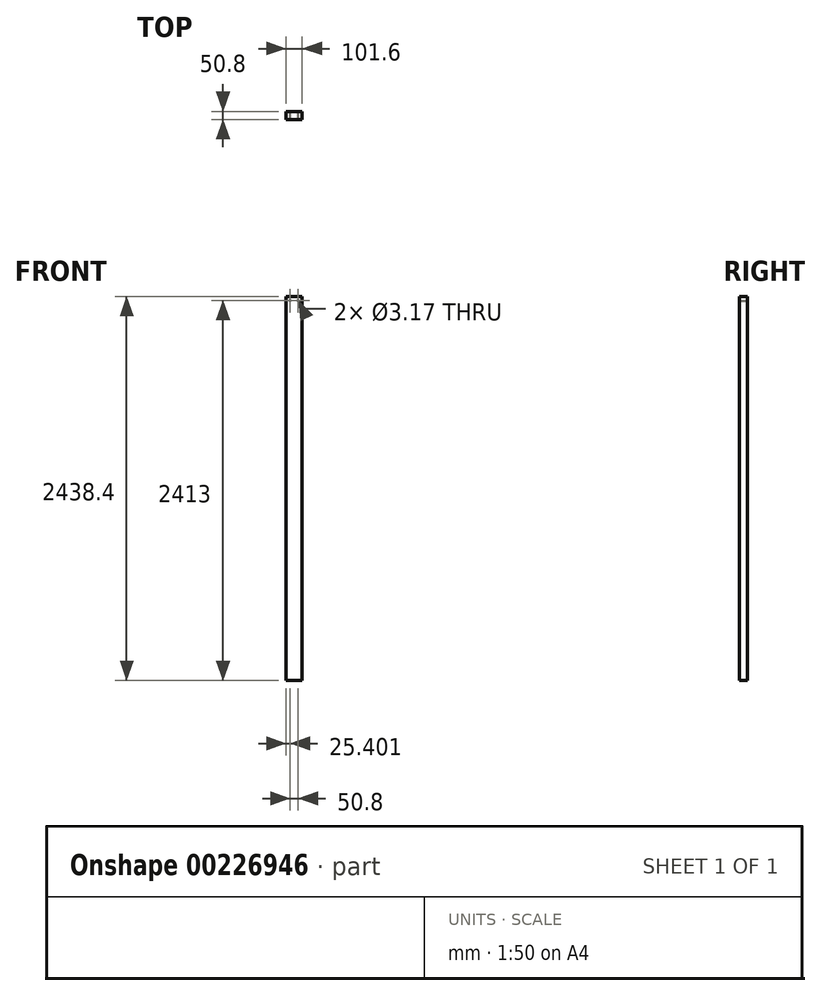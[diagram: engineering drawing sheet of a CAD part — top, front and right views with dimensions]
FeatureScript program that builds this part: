
annotation { "Feature Type Name" : "Feature", "Feature Type Description" : "" }
export const myFeature = defineFeature(function(context is Context, id is Id, definition is map)
    precondition{}
    {
        {
            var Q0;
            Q0=qCreatedBy(makeId("Front.planeOp"),FACE);
            var sketch = newSketch(context, id + "F0", { "sketchPlane" : qUnion([Q0])});
            skLineSegment(sketch, "E0.bottom", {"start": v(-276.56, 1214.25) * mm, "end": v(-174.96, 1214.25) * mm});
            skLineSegment(sketch, "E0.top", {"start": v(-276.56, -1224.15) * mm, "end": v(-174.96, -1224.15) * mm});
            skLineSegment(sketch, "E0.left", {"start": v(-276.56, 1214.25) * mm, "end": v(-276.56, -1224.15) * mm});
            skLineSegment(sketch, "E0.right", {"start": v(-174.96, 1214.25) * mm, "end": v(-174.96, -1224.15) * mm});
            skCircle(sketch, "E1", {"center": v(-251.16, 1188.85) * mm, "radius": 1.59 * mm});
            skCircle(sketch, "E2", {"center": v(-200.36, 1188.85) * mm, "radius": 1.59 * mm});
            skSolve(sketch);
        }
        {
            var Q0;
            Q0 = qSketchRegion(id + "F0", true);
            extrude(context, id + "F1", {"entities" : qUnion([Q0]), "depth" : 50.8 * mm});
        }
        {
            var Q0;
            Q0=makeQuery(id+"F0.imprint","IMPRINT",FACE,{"disambiguationData":[TD([[makeQuery(id+"F0.imprint","IMPRINT",EDGE,{"derivedFrom":sQuery(id+"F0.wireOp",EDGE,"E0.bottom")}),-1.0]])]});
            extrude(context, id + "F2", {"entities" : qUnion([Q0]), "operationType" : NewBodyOperationType.ADD, "depth" : 25.4 * mm});
        }
    });
